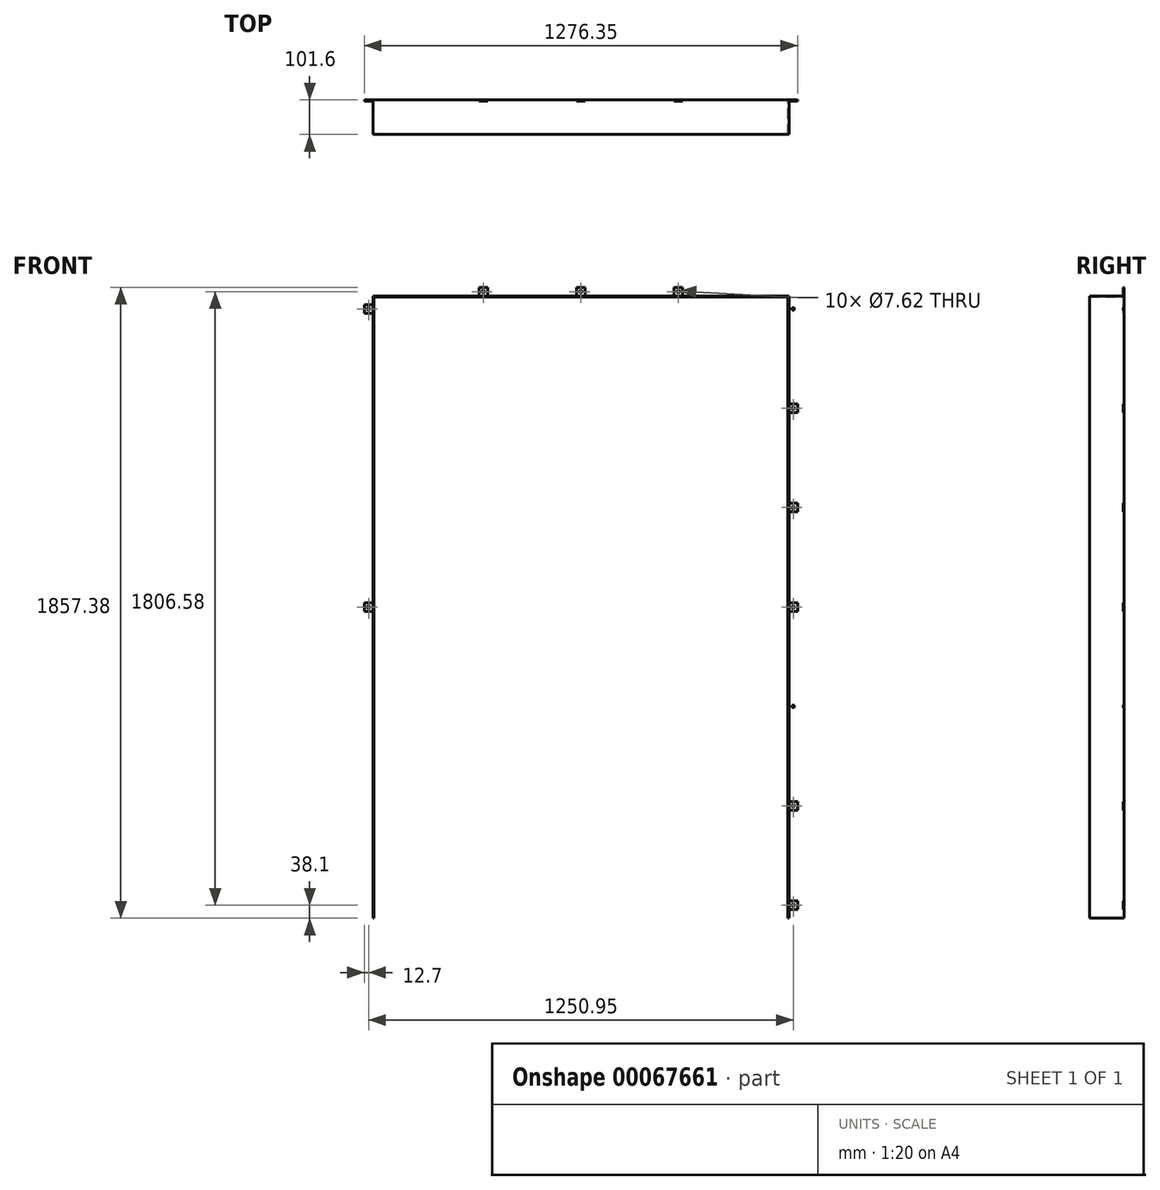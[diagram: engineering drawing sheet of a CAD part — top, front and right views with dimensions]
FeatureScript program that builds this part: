
annotation { "Feature Type Name" : "Feature", "Feature Type Description" : "" }
export const myFeature = defineFeature(function(context is Context, id is Id, definition is map)
    precondition{}
    {
        {
            var Q0;
            Q0=qCreatedBy(makeId("Front.planeOp"),FACE);
            var sketch = newSketch(context, id + "F0", { "sketchPlane" : qUnion([Q0])});
            skLineSegment(sketch, "E0", {"start": v(0, 0) * mm, "end": v(0, 1831.98) * mm});
            skLineSegment(sketch, "E1", {"start": v(0, 1831.98) * mm, "end": v(1225.55, 1831.98) * mm});
            skLineSegment(sketch, "E2", {"start": v(1225.55, 1831.98) * mm, "end": v(1225.55, 0) * mm});
            skLineSegment(sketch, "E3", {"start": v(1225.55, 0) * mm, "end": v(1222.38, 0) * mm});
            skLineSegment(sketch, "E4", {"start": v(1222.38, 0) * mm, "end": v(1222.38, 1828.8) * mm});
            skLineSegment(sketch, "E5", {"start": v(1222.38, 1828.8) * mm, "end": v(3.17, 1828.8) * mm});
            skLineSegment(sketch, "E6", {"start": v(3.18, 1828.8) * mm, "end": v(3.18, 0) * mm});
            skLineSegment(sketch, "E7", {"start": v(3.18, 0) * mm, "end": v(0, 0) * mm});
            skLineSegment(sketch, "E8", {"start": v(612.78, 1831.98) * mm, "end": v(612.78, 1828.8) * mm, "construction": true});
            skLineSegment(sketch, "E9", {"start": v(612.78, 1828.8) * mm, "end": v(612.78, -376.43) * mm, "construction": true});
            skLineSegment(sketch, "E10.bottom", {"start": v(0, 1806.57) * mm, "end": v(-25.4, 1806.57) * mm});
            skLineSegment(sketch, "E10.top", {"start": v(0, 1781.17) * mm, "end": v(-25.4, 1781.17) * mm});
            skLineSegment(sketch, "E10.left", {"start": v(0, 1806.57) * mm, "end": v(0, 1781.17) * mm});
            skLineSegment(sketch, "E10.right", {"start": v(-25.4, 1806.57) * mm, "end": v(-25.4, 1781.17) * mm});
            skLineSegment(sketch, "E11", {"start": v(-12.7, 1806.57) * mm, "end": v(-12.7, 1781.17) * mm, "construction": true});
            skLineSegment(sketch, "E12", {"start": v(-25.4, 1793.87) * mm, "end": v(0, 1793.87) * mm, "construction": true});
            skCircle(sketch, "E13", {"center": v(-12.7, 1793.87) * mm, "radius": 3.81 * mm});
            skLineSegment(sketch, "E14.left", {"start": v(0, 1513.95) * mm, "end": v(0, 1488.55) * mm});
            skLineSegment(sketch, "E15", {"start": v(-25.4, 1501.25) * mm, "end": v(0, 1501.25) * mm, "construction": true});
            skLineSegment(sketch, "E16", {"start": v(-12.7, 1513.95) * mm, "end": v(-12.7, 1488.55) * mm, "construction": true});
            skLineSegment(sketch, "E14.right", {"start": v(-25.4, 1513.95) * mm, "end": v(-25.4, 1488.55) * mm});
            skLineSegment(sketch, "E14.top", {"start": v(0, 1488.55) * mm, "end": v(-25.4, 1488.55) * mm});
            skLineSegment(sketch, "E14.bottom", {"start": v(0, 1513.95) * mm, "end": v(-25.4, 1513.95) * mm});
            skCircle(sketch, "E17", {"center": v(-12.7, 1501.25) * mm, "radius": 3.81 * mm});
            skLineSegment(sketch, "E18.left", {"start": v(0, 1221.32) * mm, "end": v(0, 1195.92) * mm});
            skLineSegment(sketch, "E19", {"start": v(-25.4, 1208.62) * mm, "end": v(0, 1208.62) * mm, "construction": true});
            skLineSegment(sketch, "E20", {"start": v(-12.7, 1221.32) * mm, "end": v(-12.7, 1195.92) * mm, "construction": true});
            skLineSegment(sketch, "E18.right", {"start": v(-25.4, 1221.32) * mm, "end": v(-25.4, 1195.92) * mm});
            skLineSegment(sketch, "E18.top", {"start": v(0, 1195.92) * mm, "end": v(-25.4, 1195.92) * mm});
            skLineSegment(sketch, "E18.bottom", {"start": v(0, 1221.32) * mm, "end": v(-25.4, 1221.32) * mm});
            skCircle(sketch, "E21", {"center": v(-12.7, 1208.62) * mm, "radius": 3.81 * mm});
            skLineSegment(sketch, "E22.left", {"start": v(0, 50.8) * mm, "end": v(0, 25.4) * mm});
            skLineSegment(sketch, "E23", {"start": v(-25.4, 38.1) * mm, "end": v(0, 38.1) * mm, "construction": true});
            skLineSegment(sketch, "E24", {"start": v(-12.7, 50.8) * mm, "end": v(-12.7, 25.4) * mm, "construction": true});
            skLineSegment(sketch, "E22.right", {"start": v(-25.4, 50.8) * mm, "end": v(-25.4, 25.4) * mm});
            skLineSegment(sketch, "E22.top", {"start": v(0, 25.4) * mm, "end": v(-25.4, 25.4) * mm});
            skLineSegment(sketch, "E22.bottom", {"start": v(0, 50.8) * mm, "end": v(-25.4, 50.8) * mm});
            skCircle(sketch, "E25", {"center": v(-12.7, 38.1) * mm, "radius": 3.81 * mm});
            skLineSegment(sketch, "E26.left", {"start": v(0, 343.43) * mm, "end": v(0, 318.03) * mm});
            skLineSegment(sketch, "E27", {"start": v(-25.4, 330.73) * mm, "end": v(0, 330.73) * mm, "construction": true});
            skLineSegment(sketch, "E28", {"start": v(-12.7, 343.43) * mm, "end": v(-12.7, 318.03) * mm, "construction": true});
            skLineSegment(sketch, "E26.right", {"start": v(-25.4, 343.43) * mm, "end": v(-25.4, 318.03) * mm});
            skLineSegment(sketch, "E26.top", {"start": v(0, 318.03) * mm, "end": v(-25.4, 318.03) * mm});
            skLineSegment(sketch, "E26.bottom", {"start": v(0, 343.43) * mm, "end": v(-25.4, 343.43) * mm});
            skCircle(sketch, "E29", {"center": v(-12.7, 330.73) * mm, "radius": 3.81 * mm});
            skLineSegment(sketch, "E30.left", {"start": v(0, 636.06) * mm, "end": v(0, 610.66) * mm});
            skLineSegment(sketch, "E31", {"start": v(-25.4, 623.36) * mm, "end": v(0, 623.36) * mm, "construction": true});
            skLineSegment(sketch, "E32", {"start": v(-12.7, 636.06) * mm, "end": v(-12.7, 610.66) * mm, "construction": true});
            skLineSegment(sketch, "E30.right", {"start": v(-25.4, 636.06) * mm, "end": v(-25.4, 610.66) * mm});
            skLineSegment(sketch, "E30.top", {"start": v(0, 610.66) * mm, "end": v(-25.4, 610.66) * mm});
            skLineSegment(sketch, "E30.bottom", {"start": v(0, 636.06) * mm, "end": v(-25.4, 636.06) * mm});
            skCircle(sketch, "E33", {"center": v(-12.7, 623.36) * mm, "radius": 3.81 * mm});
            skLineSegment(sketch, "E34.MirrorCS", {"start": v(1250.95, 1793.87) * mm, "end": v(1225.55, 1793.87) * mm, "construction": true});
            skCircle(sketch, "E35.MirrorC", {"center": v(1238.25, 1793.88) * mm, "radius": 3.81 * mm});
            skLineSegment(sketch, "E36.MirrorCS", {"start": v(1225.55, 1806.57) * mm, "end": v(1250.95, 1806.57) * mm});
            skLineSegment(sketch, "E37.MirrorCS", {"start": v(1238.25, 1806.58) * mm, "end": v(1238.25, 1781.17) * mm, "construction": true});
            skLineSegment(sketch, "E38.MirrorCS", {"start": v(1250.95, 1806.58) * mm, "end": v(1250.95, 1781.18) * mm});
            skLineSegment(sketch, "E39.MirrorCS", {"start": v(1225.55, 1806.58) * mm, "end": v(1225.55, 1781.18) * mm});
            skLineSegment(sketch, "E40.MirrorCS", {"start": v(1225.55, 1781.17) * mm, "end": v(1250.95, 1781.17) * mm});
            skLineSegment(sketch, "E41.MirrorCS", {"start": v(1250.95, 1501.25) * mm, "end": v(1225.55, 1501.25) * mm, "construction": true});
            skLineSegment(sketch, "E42.MirrorCS", {"start": v(1225.55, 1513.95) * mm, "end": v(1250.95, 1513.95) * mm});
            skCircle(sketch, "E43.MirrorC", {"center": v(1238.25, 1501.25) * mm, "radius": 3.81 * mm});
            skLineSegment(sketch, "E44.MirrorCS", {"start": v(1225.55, 1513.95) * mm, "end": v(1225.55, 1488.55) * mm});
            skLineSegment(sketch, "E45.MirrorCS", {"start": v(1238.25, 1513.95) * mm, "end": v(1238.25, 1488.55) * mm, "construction": true});
            skLineSegment(sketch, "E46.MirrorCS", {"start": v(1250.95, 1513.95) * mm, "end": v(1250.95, 1488.55) * mm});
            skLineSegment(sketch, "E47.MirrorCS", {"start": v(1225.55, 1488.55) * mm, "end": v(1250.95, 1488.55) * mm});
            skLineSegment(sketch, "E48.MirrorCS", {"start": v(1250.95, 1221.32) * mm, "end": v(1250.95, 1195.92) * mm});
            skLineSegment(sketch, "E49.MirrorCS", {"start": v(1250.95, 1208.62) * mm, "end": v(1225.55, 1208.62) * mm, "construction": true});
            skLineSegment(sketch, "E50.MirrorCS", {"start": v(1238.25, 1221.32) * mm, "end": v(1238.25, 1195.92) * mm, "construction": true});
            skCircle(sketch, "E51.MirrorC", {"center": v(1238.25, 1208.62) * mm, "radius": 3.81 * mm});
            skLineSegment(sketch, "E52.MirrorCS", {"start": v(1225.55, 1195.92) * mm, "end": v(1250.95, 1195.92) * mm});
            skLineSegment(sketch, "E53.MirrorCS", {"start": v(1225.55, 1221.32) * mm, "end": v(1225.55, 1195.92) * mm});
            skLineSegment(sketch, "E54.MirrorCS", {"start": v(1225.55, 1221.32) * mm, "end": v(1250.95, 1221.32) * mm});
            skCircle(sketch, "E55.MirrorC", {"center": v(1238.25, 623.36) * mm, "radius": 3.81 * mm});
            skLineSegment(sketch, "E56.MirrorCS", {"start": v(1225.55, 636.06) * mm, "end": v(1250.95, 636.06) * mm});
            skLineSegment(sketch, "E57.MirrorCS", {"start": v(1250.95, 623.36) * mm, "end": v(1225.55, 623.36) * mm, "construction": true});
            skLineSegment(sketch, "E58.MirrorCS", {"start": v(1238.25, 636.06) * mm, "end": v(1238.25, 610.66) * mm, "construction": true});
            skLineSegment(sketch, "E59.MirrorCS", {"start": v(1225.55, 636.06) * mm, "end": v(1225.55, 610.66) * mm});
            skLineSegment(sketch, "E60.MirrorCS", {"start": v(1225.55, 610.66) * mm, "end": v(1250.95, 610.66) * mm});
            skLineSegment(sketch, "E61.MirrorCS", {"start": v(1250.95, 636.06) * mm, "end": v(1250.95, 610.66) * mm});
            skLineSegment(sketch, "E62.MirrorCS", {"start": v(1250.95, 343.43) * mm, "end": v(1250.95, 318.03) * mm});
            skLineSegment(sketch, "E63.MirrorCS", {"start": v(1225.55, 318.03) * mm, "end": v(1250.95, 318.03) * mm});
            skLineSegment(sketch, "E64.MirrorCS", {"start": v(1238.25, 343.43) * mm, "end": v(1238.25, 318.03) * mm, "construction": true});
            skLineSegment(sketch, "E65.MirrorCS", {"start": v(1225.55, 343.43) * mm, "end": v(1250.95, 343.43) * mm});
            skLineSegment(sketch, "E66.MirrorCS", {"start": v(1250.95, 330.73) * mm, "end": v(1225.55, 330.73) * mm, "construction": true});
            skLineSegment(sketch, "E67.MirrorCS", {"start": v(1225.55, 343.43) * mm, "end": v(1225.55, 318.03) * mm});
            skCircle(sketch, "E68.MirrorC", {"center": v(1238.25, 330.73) * mm, "radius": 3.81 * mm});
            skLineSegment(sketch, "E69.MirrorCS", {"start": v(1250.95, 50.8) * mm, "end": v(1250.95, 25.4) * mm});
            skLineSegment(sketch, "E70.MirrorCS", {"start": v(1238.25, 50.8) * mm, "end": v(1238.25, 25.4) * mm, "construction": true});
            skLineSegment(sketch, "E71.MirrorCS", {"start": v(1250.95, 38.1) * mm, "end": v(1225.55, 38.1) * mm, "construction": true});
            skCircle(sketch, "E72.MirrorC", {"center": v(1238.25, 38.1) * mm, "radius": 3.81 * mm});
            skLineSegment(sketch, "E73.MirrorCS", {"start": v(1225.55, 50.8) * mm, "end": v(1250.95, 50.8) * mm});
            skLineSegment(sketch, "E74.MirrorCS", {"start": v(1225.55, 50.8) * mm, "end": v(1225.55, 25.4) * mm});
            skLineSegment(sketch, "E75.MirrorCS", {"start": v(1225.55, 25.4) * mm, "end": v(1250.95, 25.4) * mm});
            skLineSegment(sketch, "E76.bottom", {"start": v(25.4, 1831.98) * mm, "end": v(50.8, 1831.98) * mm});
            skLineSegment(sketch, "E76.top", {"start": v(25.4, 1857.38) * mm, "end": v(50.8, 1857.38) * mm});
            skLineSegment(sketch, "E76.left", {"start": v(25.4, 1831.98) * mm, "end": v(25.4, 1857.38) * mm});
            skLineSegment(sketch, "E76.right", {"start": v(50.8, 1831.98) * mm, "end": v(50.8, 1857.38) * mm});
            skLineSegment(sketch, "E77.bottom", {"start": v(1200.15, 1831.98) * mm, "end": v(1174.75, 1831.98) * mm});
            skLineSegment(sketch, "E77.top", {"start": v(1200.15, 1857.38) * mm, "end": v(1174.75, 1857.38) * mm});
            skLineSegment(sketch, "E77.left", {"start": v(1200.15, 1831.98) * mm, "end": v(1200.15, 1857.38) * mm});
            skLineSegment(sketch, "E77.right", {"start": v(1174.75, 1831.98) * mm, "end": v(1174.75, 1857.38) * mm});
            skLineSegment(sketch, "E78", {"start": v(1174.75, 1857.38) * mm, "end": v(1200.15, 1831.98) * mm, "construction": true});
            skLineSegment(sketch, "E79", {"start": v(1200.15, 1857.38) * mm, "end": v(1174.75, 1831.98) * mm, "construction": true});
            skCircle(sketch, "E80", {"center": v(1187.45, 1844.67) * mm, "radius": 3.81 * mm});
            skLineSegment(sketch, "E81", {"start": v(25.4, 1857.38) * mm, "end": v(50.8, 1831.98) * mm, "construction": true});
            skLineSegment(sketch, "E82", {"start": v(50.8, 1857.38) * mm, "end": v(25.4, 1831.98) * mm, "construction": true});
            skCircle(sketch, "E83", {"center": v(38.1, 1844.68) * mm, "radius": 3.81 * mm});
            skLineSegment(sketch, "E84", {"start": v(312.74, 1844.68) * mm, "end": v(338.14, 1844.68) * mm, "construction": true});
            skCircle(sketch, "E85", {"center": v(325.44, 1844.68) * mm, "radius": 3.81 * mm});
            skLineSegment(sketch, "E86.left", {"start": v(338.14, 1857.38) * mm, "end": v(338.14, 1831.98) * mm});
            skLineSegment(sketch, "E86.top", {"start": v(338.14, 1831.98) * mm, "end": v(312.74, 1831.98) * mm});
            skLineSegment(sketch, "E86.bottom", {"start": v(338.14, 1857.38) * mm, "end": v(312.74, 1857.38) * mm});
            skLineSegment(sketch, "E87", {"start": v(325.44, 1857.38) * mm, "end": v(325.44, 1831.98) * mm, "construction": true});
            skLineSegment(sketch, "E86.right", {"start": v(312.74, 1857.38) * mm, "end": v(312.74, 1831.98) * mm});
            skLineSegment(sketch, "E88", {"start": v(600.08, 1844.68) * mm, "end": v(625.48, 1844.68) * mm, "construction": true});
            skCircle(sketch, "E89", {"center": v(612.78, 1844.67) * mm, "radius": 3.81 * mm});
            skLineSegment(sketch, "E90.left", {"start": v(625.48, 1857.38) * mm, "end": v(625.48, 1831.97) * mm});
            skLineSegment(sketch, "E90.top", {"start": v(625.47, 1831.98) * mm, "end": v(600.08, 1831.98) * mm});
            skLineSegment(sketch, "E90.bottom", {"start": v(625.47, 1857.38) * mm, "end": v(600.08, 1857.38) * mm});
            skLineSegment(sketch, "E91", {"start": v(612.78, 1857.38) * mm, "end": v(612.78, 1831.98) * mm, "construction": true});
            skLineSegment(sketch, "E90.right", {"start": v(600.08, 1857.38) * mm, "end": v(600.08, 1831.98) * mm});
            skLineSegment(sketch, "E92", {"start": v(887.41, 1844.68) * mm, "end": v(912.81, 1844.68) * mm, "construction": true});
            skCircle(sketch, "E93", {"center": v(900.11, 1844.67) * mm, "radius": 3.81 * mm});
            skLineSegment(sketch, "E94.left", {"start": v(912.81, 1857.38) * mm, "end": v(912.81, 1831.97) * mm});
            skLineSegment(sketch, "E94.top", {"start": v(912.81, 1831.98) * mm, "end": v(887.41, 1831.98) * mm});
            skLineSegment(sketch, "E94.bottom", {"start": v(912.81, 1857.38) * mm, "end": v(887.41, 1857.38) * mm});
            skLineSegment(sketch, "E95", {"start": v(900.11, 1857.38) * mm, "end": v(900.11, 1831.98) * mm, "construction": true});
            skLineSegment(sketch, "E94.right", {"start": v(887.41, 1857.38) * mm, "end": v(887.41, 1831.97) * mm});
            skLineSegment(sketch, "E96.top", {"start": v(0, 903.29) * mm, "end": v(-25.4, 903.29) * mm});
            skLineSegment(sketch, "E97", {"start": v(-12.7, 928.69) * mm, "end": v(-12.7, 903.29) * mm, "construction": true});
            skCircle(sketch, "E98", {"center": v(-12.7, 915.99) * mm, "radius": 3.81 * mm});
            skLineSegment(sketch, "E99", {"start": v(-25.4, 915.99) * mm, "end": v(0, 915.99) * mm, "construction": true});
            skLineSegment(sketch, "E96.left", {"start": v(0, 928.69) * mm, "end": v(0, 903.29) * mm});
            skLineSegment(sketch, "E96.bottom", {"start": v(0, 928.69) * mm, "end": v(-25.4, 928.69) * mm});
            skLineSegment(sketch, "E96.right", {"start": v(-25.4, 928.69) * mm, "end": v(-25.4, 903.29) * mm});
            skLineSegment(sketch, "E100", {"start": v(-12.7, 38.1) * mm, "end": v(-12.7, 330.73) * mm, "construction": true});
            skLineSegment(sketch, "E101", {"start": v(-12.7, 330.73) * mm, "end": v(-12.7, 623.36) * mm, "construction": true});
            skLineSegment(sketch, "E102", {"start": v(-12.7, 623.36) * mm, "end": v(-12.7, 915.99) * mm, "construction": true});
            skLineSegment(sketch, "E103", {"start": v(-12.7, 915.99) * mm, "end": v(-12.7, 1208.62) * mm, "construction": true});
            skLineSegment(sketch, "E104", {"start": v(-12.7, 1208.62) * mm, "end": v(-12.7, 1501.25) * mm, "construction": true});
            skLineSegment(sketch, "E105", {"start": v(-12.7, 1793.87) * mm, "end": v(-12.7, 1501.25) * mm, "construction": true});
            skLineSegment(sketch, "E106.MirrorCS", {"start": v(1238.25, 928.69) * mm, "end": v(1238.25, 903.29) * mm, "construction": true});
            skLineSegment(sketch, "E107.MirrorCS", {"start": v(1250.95, 915.99) * mm, "end": v(1225.55, 915.99) * mm, "construction": true});
            skLineSegment(sketch, "E108.MirrorCS", {"start": v(1225.55, 928.69) * mm, "end": v(1250.95, 928.69) * mm});
            skCircle(sketch, "E109.MirrorC", {"center": v(1238.25, 915.99) * mm, "radius": 3.81 * mm});
            skLineSegment(sketch, "E110.MirrorCS", {"start": v(1225.55, 903.29) * mm, "end": v(1250.95, 903.29) * mm});
            skLineSegment(sketch, "E111.MirrorCS", {"start": v(1250.95, 928.69) * mm, "end": v(1250.95, 903.29) * mm});
            skLineSegment(sketch, "E112.MirrorCS", {"start": v(1225.55, 928.69) * mm, "end": v(1225.55, 903.29) * mm});
            skLineSegment(sketch, "E113", {"start": v(38.1, 1844.67) * mm, "end": v(325.44, 1844.68) * mm, "construction": true});
            skLineSegment(sketch, "E114", {"start": v(325.44, 1844.67) * mm, "end": v(612.78, 1844.67) * mm, "construction": true});
            skLineSegment(sketch, "E115", {"start": v(612.78, 1844.67) * mm, "end": v(900.11, 1844.67) * mm, "construction": true});
            skLineSegment(sketch, "E116", {"start": v(900.11, 1844.67) * mm, "end": v(1187.45, 1844.67) * mm, "construction": true});
            skSolve(sketch);
        }
        {
            var Q0;
            {var subQ15=sQuery(id+"F0.wireOp",EDGE,"E1");Q0=makeQuery(id+"F0.imprint","IMPRINT",FACE,{"disambiguationData":[TD([[makeQuery(id+"F0.imprint","IMPRINT",EDGE,{"derivedFrom":subQ15}),-1.0]])]});}
            extrude(context, id + "F1", {"entities" : qUnion([Q0]), "depth" : 101.6 * mm});
        }
        {
            var Q0;
            Q0=makeQuery(id+"F0.imprint","IMPRINT",FACE,{"disambiguationData":[TD([[makeQuery(id+"F0.imprint","IMPRINT",EDGE,{"derivedFrom":sQuery(id+"F0.wireOp",EDGE,"E69.MirrorCS")}),-1.0]])]});
            var Q1;
            Q1=makeQuery(id+"F0.imprint","IMPRINT",FACE,{"disambiguationData":[TD([[makeQuery(id+"F0.imprint","IMPRINT",EDGE,{"derivedFrom":sQuery(id+"F0.wireOp",EDGE,"E62.MirrorCS")}),-1.0]])]});
            var Q2;
            Q2=makeQuery(id+"F0.imprint","IMPRINT",FACE,{"disambiguationData":[TD([[makeQuery(id+"F0.imprint","IMPRINT",EDGE,{"derivedFrom":sQuery(id+"F0.wireOp",EDGE,"E55.MirrorC")}),1.0]])]});
            var Q3;
            Q3=makeQuery(id+"F0.imprint","IMPRINT",FACE,{"disambiguationData":[TD([[makeQuery(id+"F0.imprint","IMPRINT",EDGE,{"derivedFrom":sQuery(id+"F0.wireOp",EDGE,"E48.MirrorCS")}),-1.0]])]});
            var Q4;
            Q4=makeQuery(id+"F0.imprint","IMPRINT",FACE,{"disambiguationData":[TD([[makeQuery(id+"F0.imprint","IMPRINT",EDGE,{"derivedFrom":sQuery(id+"F0.wireOp",EDGE,"E42.MirrorCS")}),-1.0]])]});
            var Q5;
            Q5=makeQuery(id+"F0.imprint","IMPRINT",FACE,{"disambiguationData":[TD([[makeQuery(id+"F0.imprint","IMPRINT",EDGE,{"derivedFrom":sQuery(id+"F0.wireOp",EDGE,"E35.MirrorC")}),1.0]])]});
            var Q6;
            Q6=makeQuery(id+"F0.imprint","IMPRINT",FACE,{"disambiguationData":[TD([[makeQuery(id+"F0.imprint","IMPRINT",EDGE,{"derivedFrom":sQuery(id+"F0.wireOp",EDGE,"E10.bottom")}),1.0]])]});
            var Q7;
            Q7=makeQuery(id+"F0.imprint","IMPRINT",FACE,{"disambiguationData":[TD([[makeQuery(id+"F0.imprint","IMPRINT",EDGE,{"derivedFrom":sQuery(id+"F0.wireOp",EDGE,"E14.left")}),-1.0]])]});
            var Q8;
            Q8=makeQuery(id+"F0.imprint","IMPRINT",FACE,{"disambiguationData":[TD([[makeQuery(id+"F0.imprint","IMPRINT",EDGE,{"derivedFrom":sQuery(id+"F0.wireOp",EDGE,"E18.left")}),-1.0]])]});
            var Q9;
            Q9=makeQuery(id+"F0.imprint","IMPRINT",FACE,{"disambiguationData":[TD([[makeQuery(id+"F0.imprint","IMPRINT",EDGE,{"derivedFrom":sQuery(id+"F0.wireOp",EDGE,"E30.left")}),-1.0]])]});
            var Q10;
            Q10=makeQuery(id+"F0.imprint","IMPRINT",FACE,{"disambiguationData":[TD([[makeQuery(id+"F0.imprint","IMPRINT",EDGE,{"derivedFrom":sQuery(id+"F0.wireOp",EDGE,"E26.left")}),-1.0]])]});
            var Q11;
            Q11=makeQuery(id+"F0.imprint","IMPRINT",FACE,{"disambiguationData":[TD([[makeQuery(id+"F0.imprint","IMPRINT",EDGE,{"derivedFrom":sQuery(id+"F0.wireOp",EDGE,"E22.left")}),-1.0]])]});
            var Q12;
            Q12=makeQuery(id+"F0.imprint","IMPRINT",FACE,{"disambiguationData":[TD([[makeQuery(id+"F0.imprint","IMPRINT",EDGE,{"derivedFrom":sQuery(id+"F0.wireOp",EDGE,"E76.bottom")}),1.0]])]});
            var Q13;
            Q13=makeQuery(id+"F0.imprint","IMPRINT",FACE,{"disambiguationData":[TD([[makeQuery(id+"F0.imprint","IMPRINT",EDGE,{"derivedFrom":sQuery(id+"F0.wireOp",EDGE,"e8b36b14-baf5-47ac-a38b-4cfdd02c8466.bottom")}),1.0]])]});
            var Q14;
            Q14=makeQuery(id+"F0.imprint","IMPRINT",FACE,{"disambiguationData":[TD([[makeQuery(id+"F0.imprint","IMPRINT",EDGE,{"derivedFrom":sQuery(id+"F0.wireOp",EDGE,"E77.bottom")}),-1.0]])]});
            var Q15;
            Q15=makeQuery(id+"F0.imprint","IMPRINT",FACE,{"disambiguationData":[TD([[makeQuery(id+"F0.imprint","IMPRINT",EDGE,{"derivedFrom":sQuery(id+"F0.wireOp",EDGE,"E85")}),-1.0]])]});
            var Q16;
            Q16=makeQuery(id+"F0.imprint","IMPRINT",FACE,{"disambiguationData":[TD([[makeQuery(id+"F0.imprint","IMPRINT",EDGE,{"derivedFrom":sQuery(id+"F0.wireOp",EDGE,"70c7b6a7-01ed-414b-a764-cb33e45972b0")}),-1.0]])]});
            var Q17;
            Q17=makeQuery(id+"F0.imprint","IMPRINT",FACE,{"disambiguationData":[TD([[makeQuery(id+"F0.imprint","IMPRINT",EDGE,{"derivedFrom":sQuery(id+"F0.wireOp",EDGE,"E89")}),-1.0]])]});
            var Q18;
            Q18=makeQuery(id+"F0.imprint","IMPRINT",FACE,{"disambiguationData":[TD([[makeQuery(id+"F0.imprint","IMPRINT",EDGE,{"derivedFrom":sQuery(id+"F0.wireOp",EDGE,"E93")}),-1.0]])]});
            var Q19;
            Q19=makeQuery(id+"F0.imprint","IMPRINT",FACE,{"disambiguationData":[TD([[makeQuery(id+"F0.imprint","IMPRINT",EDGE,{"derivedFrom":sQuery(id+"F0.wireOp",EDGE,"E96.top")}),-1.0]])]});
            var Q20;
            Q20=makeQuery(id+"F0.imprint","IMPRINT",FACE,{"disambiguationData":[TD([[makeQuery(id+"F0.imprint","IMPRINT",EDGE,{"derivedFrom":sQuery(id+"F0.wireOp",EDGE,"E110.MirrorCS")}),1.0]])]});
            extrude(context, id + "F2", {"entities" : qUnion([Q0, Q1, Q2, Q3, Q4, Q5, Q6, Q7, Q8, Q9, Q10, Q11, Q12, Q13, Q14, Q15, Q16, Q17, Q18, Q19, Q20]), "operationType" : NewBodyOperationType.ADD, "depth" : 3.17 * mm});
        }
    });
